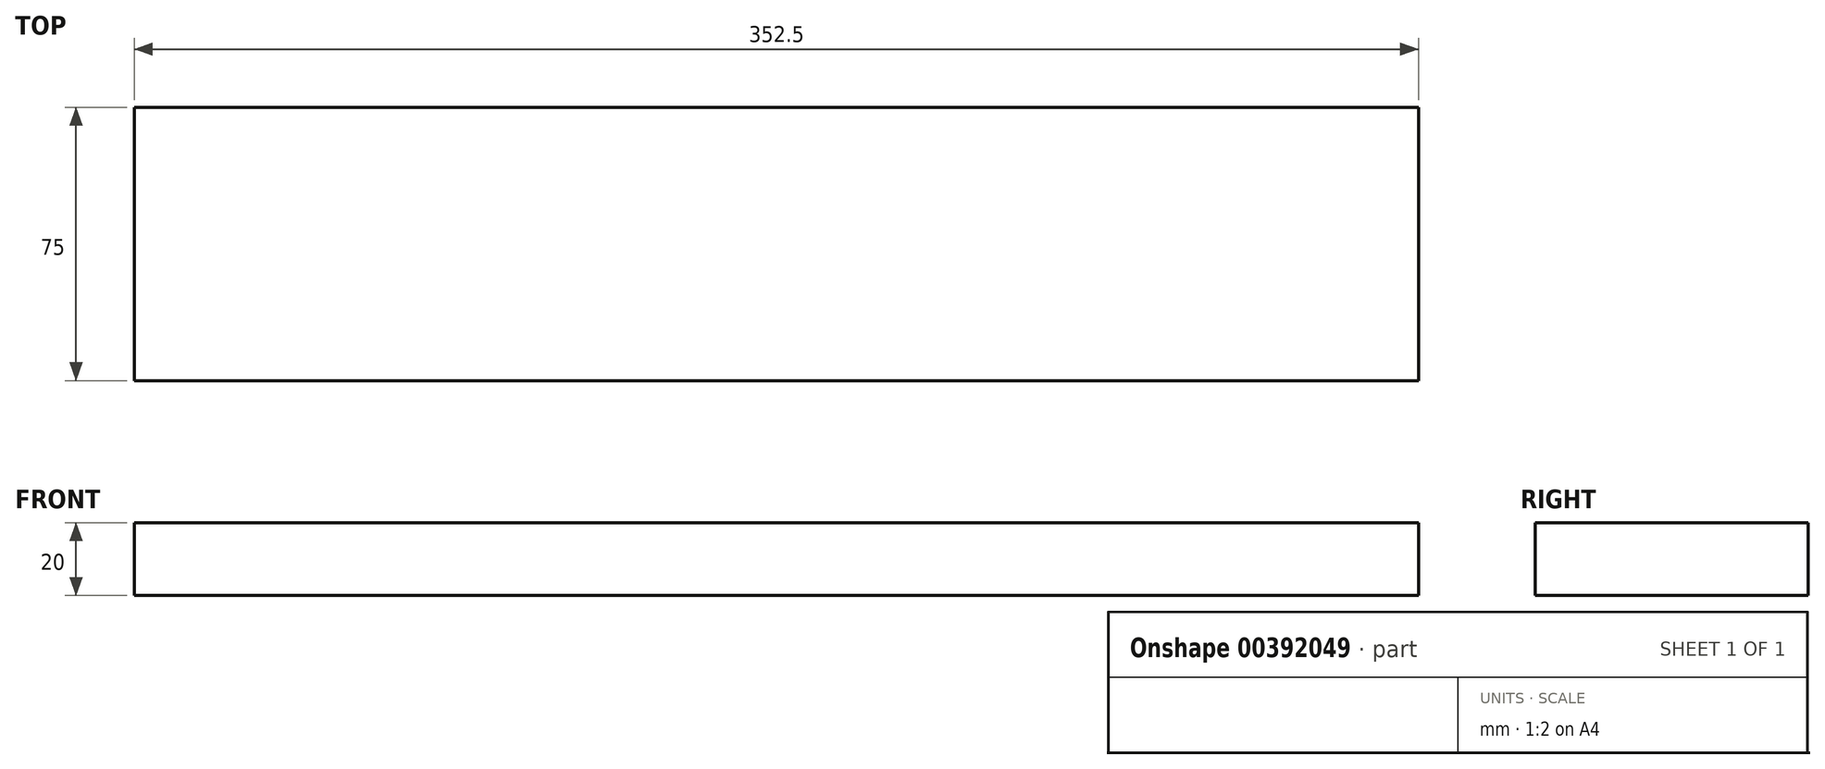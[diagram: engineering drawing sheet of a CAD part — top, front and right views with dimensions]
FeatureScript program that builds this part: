
annotation { "Feature Type Name" : "Feature", "Feature Type Description" : "" }
export const myFeature = defineFeature(function(context is Context, id is Id, definition is map)
    precondition{}
    {
        {
            var Q0;
            Q0=qCreatedBy(makeId("Right.planeOp"),FACE);
            var sketch = newSketch(context, id + "F0", { "sketchPlane" : qUnion([Q0])});
            skLineSegment(sketch, "E0.bottom", {"start": v(37.5, 10) * mm, "end": v(-37.5, 10) * mm});
            skLineSegment(sketch, "E0.top", {"start": v(37.5, -10) * mm, "end": v(-37.5, -10) * mm});
            skLineSegment(sketch, "E0.left", {"start": v(37.5, 10) * mm, "end": v(37.5, -10) * mm});
            skLineSegment(sketch, "E0.right", {"start": v(-37.5, 10) * mm, "end": v(-37.5, -10) * mm});
            skPoint(sketch, "E0.middle", {"position": v(0, 0) * mm});
            skSolve(sketch);
        }
        {
            var Q0;
            Q0=makeQuery(id+"F0.imprint","IMPRINT",FACE,{"disambiguationData":[TD([[makeQuery(id+"F0.imprint","IMPRINT",EDGE,{"derivedFrom":sQuery(id+"F0.wireOp",EDGE,"E0.bottom")}),1.0]])]});
            var Q1;
            Q1 = qSketchRegion(id + "F0", true);
            extrude(context, id + "F1", {"entities" : qUnion([Q0, Q1]), "endBound" : BoundingType.SYMMETRIC, "depth" : 352.5 * mm});
        }
    });
